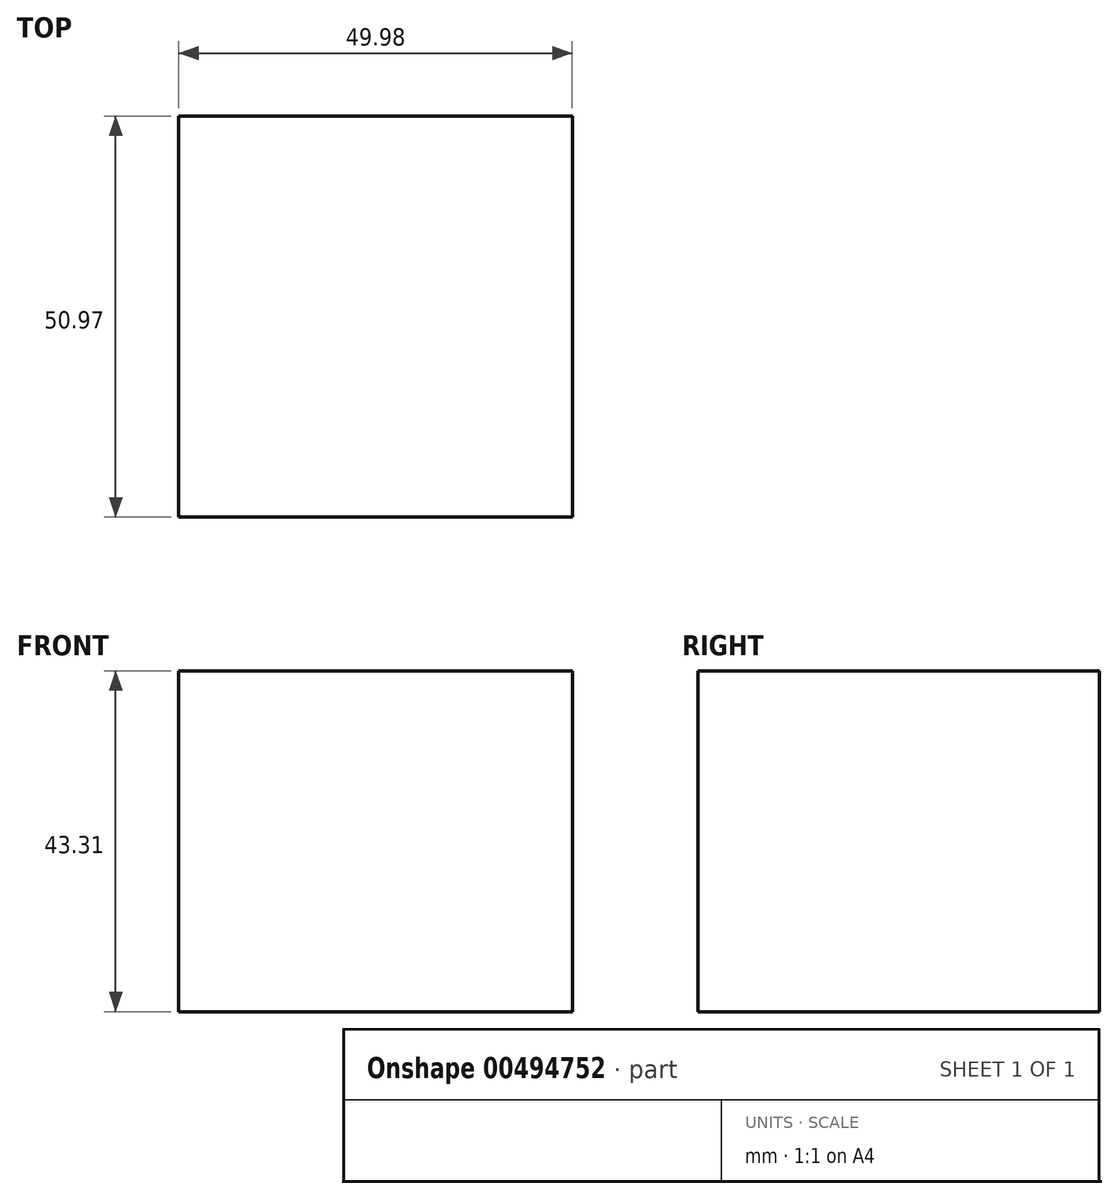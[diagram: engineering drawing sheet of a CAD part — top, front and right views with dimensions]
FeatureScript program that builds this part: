
annotation { "Feature Type Name" : "Feature", "Feature Type Description" : "" }
export const myFeature = defineFeature(function(context is Context, id is Id, definition is map)
    precondition{}
    {
        {
            var Q0;
            Q0=qCreatedBy(makeId("Front.planeOp"),FACE);
            var sketch = newSketch(context, id + "F0", { "sketchPlane" : qUnion([Q0])});
            skLineSegment(sketch, "E0.bottom", {"start": v(0, 0) * mm, "end": v(49.98, 0) * mm});
            skLineSegment(sketch, "E0.top", {"start": v(0, -43.3) * mm, "end": v(49.98, -43.3) * mm});
            skLineSegment(sketch, "E0.left", {"start": v(0, 0) * mm, "end": v(0, -43.3) * mm});
            skLineSegment(sketch, "E0.right", {"start": v(49.98, 0) * mm, "end": v(49.98, -43.3) * mm});
            skLineSegment(sketch, "E1.bottom", {"start": v(49.98, -21.65) * mm, "end": v(49.98, -21.65) * mm});
            skLineSegment(sketch, "E1.top", {"start": v(49.98, -6.68) * mm, "end": v(49.98, -6.68) * mm});
            skLineSegment(sketch, "E1.left", {"start": v(49.98, -21.65) * mm, "end": v(49.98, -6.68) * mm});
            skLineSegment(sketch, "E1.right", {"start": v(49.98, -21.65) * mm, "end": v(49.98, -6.68) * mm});
            skSolve(sketch);
        }
        {
            var Q0;
            {var subQ1=sQuery(id+"F0.wireOp",EDGE,"E0.bottom");Q0=makeQuery(id+"F0.imprint","IMPRINT",FACE,{"disambiguationData":[TD([[makeQuery(id+"F0.imprint","IMPRINT",EDGE,{"derivedFrom":subQ1}),-1.0]])]});}
            extrude(context, id + "F1", {"entities" : qUnion([Q0]), "oppositeDirection" : true, "depth" : 50.97 * mm});
        }
        {
            var Q0;
            Q0=makeQuery(id+"F1.opExtrude","CAP_FACE",FACE,{"disambiguationData":[OSD([sQuery(id+"F0.wireOp",EDGE,"E0.bottom"),sQuery(id+"F0.wireOp",EDGE,"E0.top"),sQuery(id+"F0.wireOp",EDGE,"E0.left"),sQuery(id+"F0.wireOp",EDGE,"E0.right"),sQuery(id+"F0.wireOp",EDGE,"E1.right")])],"isStart":false});
            var sketch = newSketch(context, id + "F2", { "sketchPlane" : qUnion([Q0])});
            skCircle(sketch, "E2", {"center": v(-24.32, -21.34) * mm, "radius": 14.93 * mm});
            skSolve(sketch);
        }
        {
            var Q0;
            Q0=sQuery(id+"F2.wireOp",EDGE,"E2");
            extrude(context, id + "F3", {"bodyType" : ToolBodyType.SURFACE, "surfaceEntities" : qUnion([Q0]), "oppositeDirection" : true, "depth" : 50.98 * mm});
        }
    });
